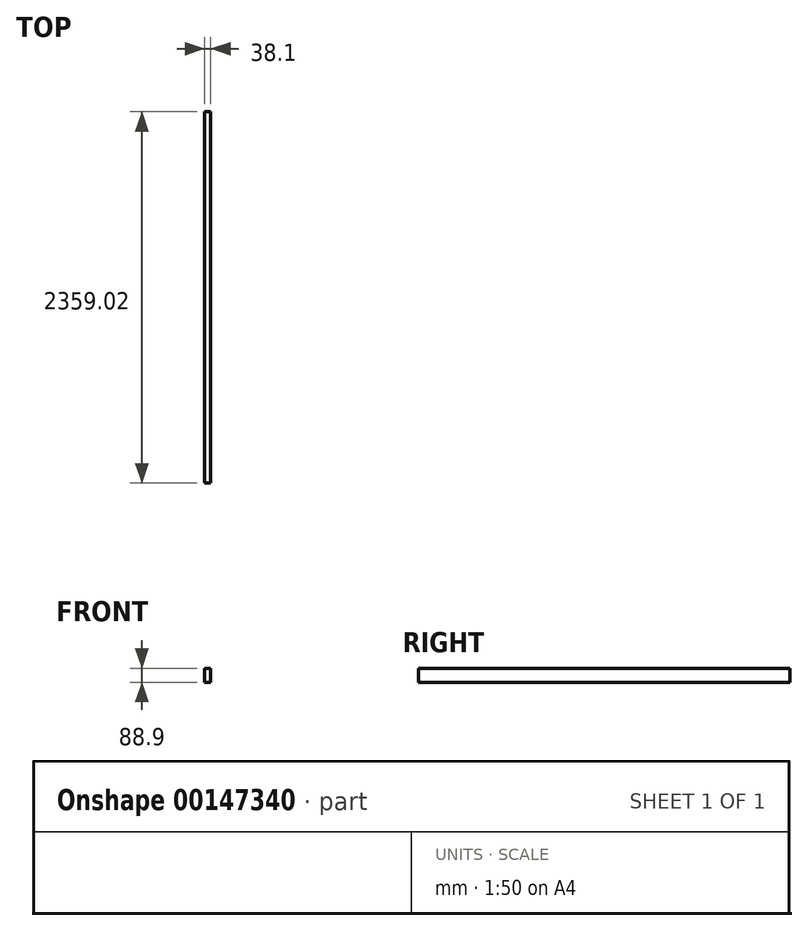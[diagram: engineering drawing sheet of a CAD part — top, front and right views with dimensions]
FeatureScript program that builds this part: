
annotation { "Feature Type Name" : "Feature", "Feature Type Description" : "" }
export const myFeature = defineFeature(function(context is Context, id is Id, definition is map)
    precondition{}
    {
        {
            var Q0;
            Q0=qCreatedBy(makeId("Front.planeOp"),FACE);
            var sketch = newSketch(context, id + "F0", { "sketchPlane" : qUnion([Q0])});
            skLineSegment(sketch, "E0.bottom", {"start": v(-18, 55.77) * mm, "end": v(20.1, 55.77) * mm});
            skLineSegment(sketch, "E0.top", {"start": v(-18, -33.13) * mm, "end": v(20.1, -33.13) * mm});
            skLineSegment(sketch, "E0.left", {"start": v(-18, 55.77) * mm, "end": v(-18, -33.13) * mm});
            skLineSegment(sketch, "E0.right", {"start": v(20.1, 55.77) * mm, "end": v(20.1, -33.13) * mm});
            skSolve(sketch);
        }
        {
            var Q0;
            Q0=qSketchRegion(id+"F0",true);
            extrude(context, id + "F1", {"entities" : qUnion([Q0]), "endBound" : BoundingType.SYMMETRIC, "depth" : 2359.03 * mm});
        }
    });
